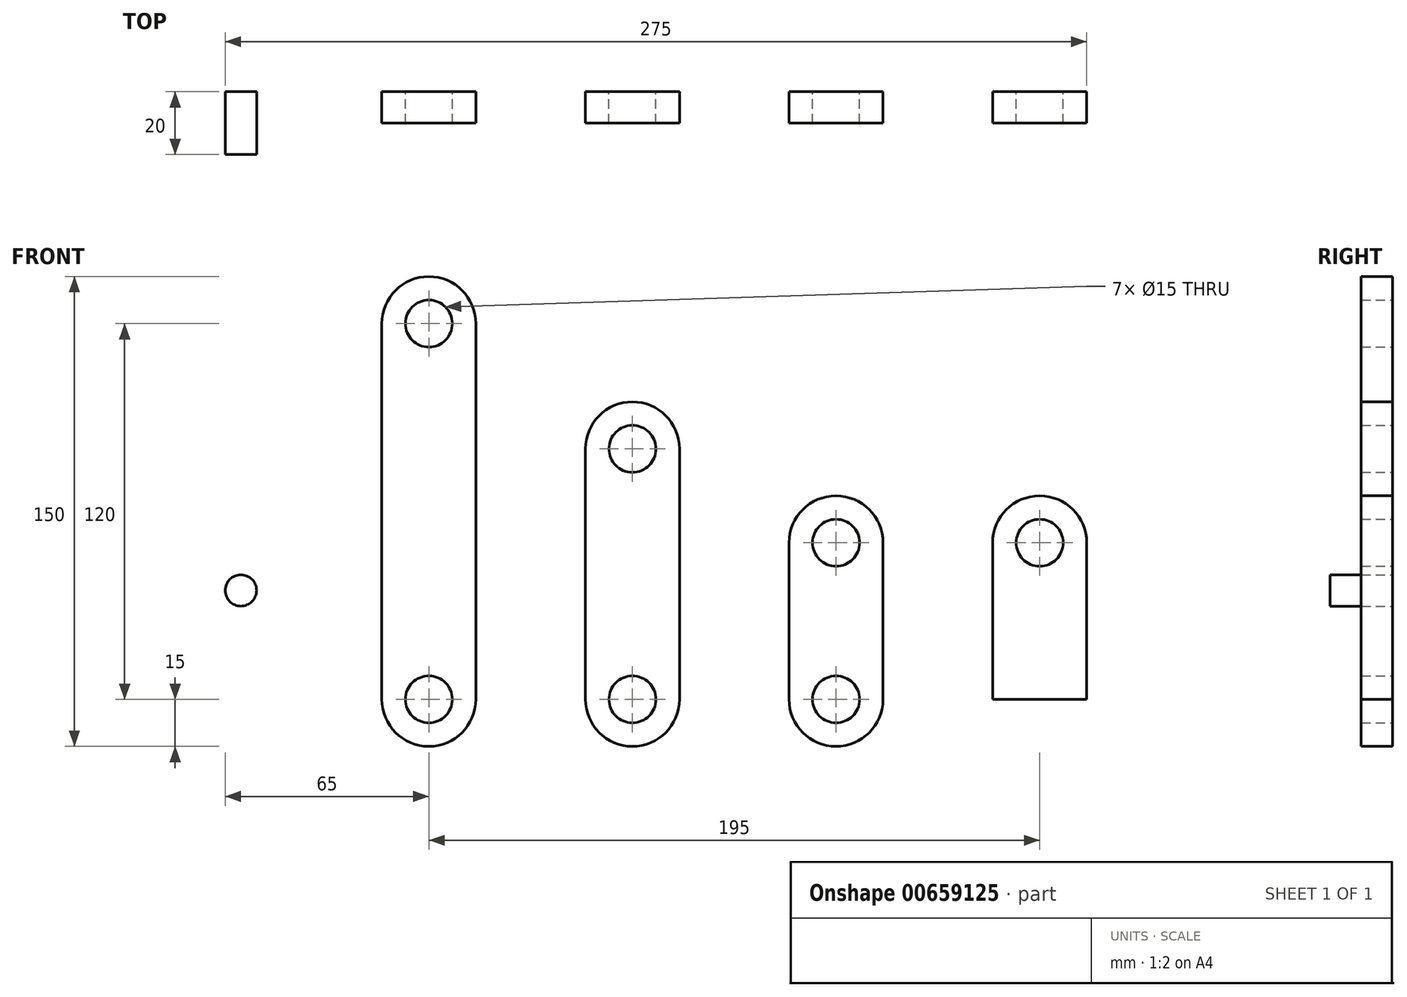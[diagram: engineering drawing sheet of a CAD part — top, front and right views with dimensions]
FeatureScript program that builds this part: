
annotation { "Feature Type Name" : "Feature", "Feature Type Description" : "" }
export const myFeature = defineFeature(function(context is Context, id is Id, definition is map)
    precondition{}
    {
        {
            assignVariable(context, id + "F0", {"name" : "thickness", "anyValue" : 10});
        }
        {
            var Q0;
            Q0=qCreatedBy(makeId("Front.planeOp"),FACE);
            var sketch = newSketch(context, id + "F1", { "sketchPlane" : qUnion([Q0])});
            skLineSegment(sketch, "E0", {"start": v(0, 0) * mm, "end": v(30, 0) * mm});
            skLineSegment(sketch, "E1", {"start": v(0, 0) * mm, "end": v(0, 50) * mm});
            skArc(sketch, "E2", {"start": v(30, 50) * mm, "mid": v(15, 65) * mm, "end": v(0, 50) * mm});
            skPoint(sketch, "E2.centerSnap0", {"position": v(15, 0) * mm});
            skCircle(sketch, "E3", {"center": v(15, 50) * mm, "radius": 7.5 * mm});
            skLineSegment(sketch, "E4", {"start": v(30, 50) * mm, "end": v(30, 0) * mm});
            skSolve(sketch);
        }
        {
            var Q0;
            Q0=makeQuery(id+"F1.imprint","IMPRINT",FACE,{"disambiguationData":[TD([[makeQuery(id+"F1.imprint","IMPRINT",EDGE,{"derivedFrom":sQuery(id+"F1.wireOp",EDGE,"E0")}),1.0]])]});
            extrude(context, id + "F2", {"entities" : qUnion([Q0]), "depth" : (getVariable(context, 'thickness')) * mm, "offsetDistance" : 25 * mm});
        }
        {
            var Q0;
            Q0=qCreatedBy(makeId("Front.planeOp"),FACE);
            var sketch = newSketch(context, id + "F3", { "sketchPlane" : qUnion([Q0])});
            skArc(sketch, "E5", {"start": v(-65, 0) * mm, "mid": v(-50, -15) * mm, "end": v(-35, 0) * mm});
            skCircle(sketch, "E6", {"center": v(-50, 0) * mm, "radius": 7.5 * mm});
            skLineSegment(sketch, "E7", {"start": v(-65, 0) * mm, "end": v(-65, 50) * mm});
            skArc(sketch, "E8", {"start": v(-35, 50) * mm, "mid": v(-50, 65) * mm, "end": v(-65, 50) * mm});
            skCircle(sketch, "E9", {"center": v(-50, 50) * mm, "radius": 7.5 * mm});
            skLineSegment(sketch, "E10", {"start": v(-35, 50) * mm, "end": v(-35, 0) * mm});
            skSolve(sketch);
        }
        {
            var Q0;
            Q0=makeQuery(id+"F3.imprint","IMPRINT",FACE,{"disambiguationData":[TD([[makeQuery(id+"F3.imprint","IMPRINT",EDGE,{"derivedFrom":sQuery(id+"F3.wireOp",EDGE,"E5")}),1.0]])]});
            extrude(context, id + "F4", {"entities" : qUnion([Q0]), "depth" : (getVariable(context, 'thickness')) * mm, "offsetDistance" : 25 * mm});
        }
        {
            var Q0;
            Q0=qCreatedBy(makeId("Front.planeOp"),FACE);
            var sketch = newSketch(context, id + "F5", { "sketchPlane" : qUnion([Q0])});
            skArc(sketch, "E11", {"start": v(-130, 0) * mm, "mid": v(-115, -15) * mm, "end": v(-100, 0) * mm});
            skCircle(sketch, "E12", {"center": v(-115, 0) * mm, "radius": 7.5 * mm});
            skLineSegment(sketch, "E13", {"start": v(-130, 0) * mm, "end": v(-130, 80) * mm});
            skArc(sketch, "E14", {"start": v(-100, 80) * mm, "mid": v(-115, 95) * mm, "end": v(-130, 80) * mm});
            skCircle(sketch, "E15", {"center": v(-115, 80) * mm, "radius": 7.5 * mm});
            skLineSegment(sketch, "E16", {"start": v(-100, 80) * mm, "end": v(-100, 0) * mm});
            skSolve(sketch);
        }
        {
            var Q0;
            Q0=makeQuery(id+"F5.imprint","IMPRINT",FACE,{"disambiguationData":[TD([[makeQuery(id+"F5.imprint","IMPRINT",EDGE,{"derivedFrom":sQuery(id+"F5.wireOp",EDGE,"E11")}),1.0]])]});
            extrude(context, id + "F6", {"entities" : qUnion([Q0]), "depth" : (getVariable(context, 'thickness')) * mm, "offsetDistance" : 25 * mm});
        }
        {
            var Q0;
            Q0=qCreatedBy(makeId("Front.planeOp"),FACE);
            var sketch = newSketch(context, id + "F7", { "sketchPlane" : qUnion([Q0])});
            skArc(sketch, "E17", {"start": v(-195, 0) * mm, "mid": v(-180, -15) * mm, "end": v(-165, 0) * mm});
            skCircle(sketch, "E18", {"center": v(-180, 0) * mm, "radius": 7.5 * mm});
            skLineSegment(sketch, "E19", {"start": v(-195, 0) * mm, "end": v(-195, 120) * mm});
            skArc(sketch, "E20", {"start": v(-165, 120) * mm, "mid": v(-180, 135) * mm, "end": v(-195, 120) * mm});
            skCircle(sketch, "E21", {"center": v(-180, 120) * mm, "radius": 7.5 * mm});
            skLineSegment(sketch, "E22", {"start": v(-165, 120) * mm, "end": v(-165, 0) * mm});
            skSolve(sketch);
        }
        {
            var Q0;
            Q0=makeQuery(id+"F7.imprint","IMPRINT",FACE,{"disambiguationData":[TD([[makeQuery(id+"F7.imprint","IMPRINT",EDGE,{"derivedFrom":sQuery(id+"F7.wireOp",EDGE,"E17")}),1.0]])]});
            extrude(context, id + "F8", {"entities" : qUnion([Q0]), "depth" : (getVariable(context, 'thickness')) * mm, "offsetDistance" : 25 * mm});
        }
        {
            var Q0;
            Q0=qCreatedBy(makeId("Front.planeOp"),FACE);
            var sketch = newSketch(context, id + "F9", { "sketchPlane" : qUnion([Q0])});
            skCircle(sketch, "E23", {"center": v(-240, 34.78) * mm, "radius": 5 * mm});
            skSolve(sketch);
        }
        {
            var Q0;
            Q0=makeQuery(id+"F9.imprint","IMPRINT",FACE,{"disambiguationData":[TD([[makeQuery(id+"F9.imprint","IMPRINT",EDGE,{"derivedFrom":sQuery(id+"F9.wireOp",EDGE,"E23")}),1.0]])]});
            var Q1;
            Q1=sQuery(id+"F9.wireOp",EDGE,"E23");
            extrude(context, id + "F10", {"entities" : qUnion([Q0]), "surfaceEntities" : qUnion([Q1]), "depth" : 20 * mm, "offsetDistance" : 25 * mm});
        }
    });
